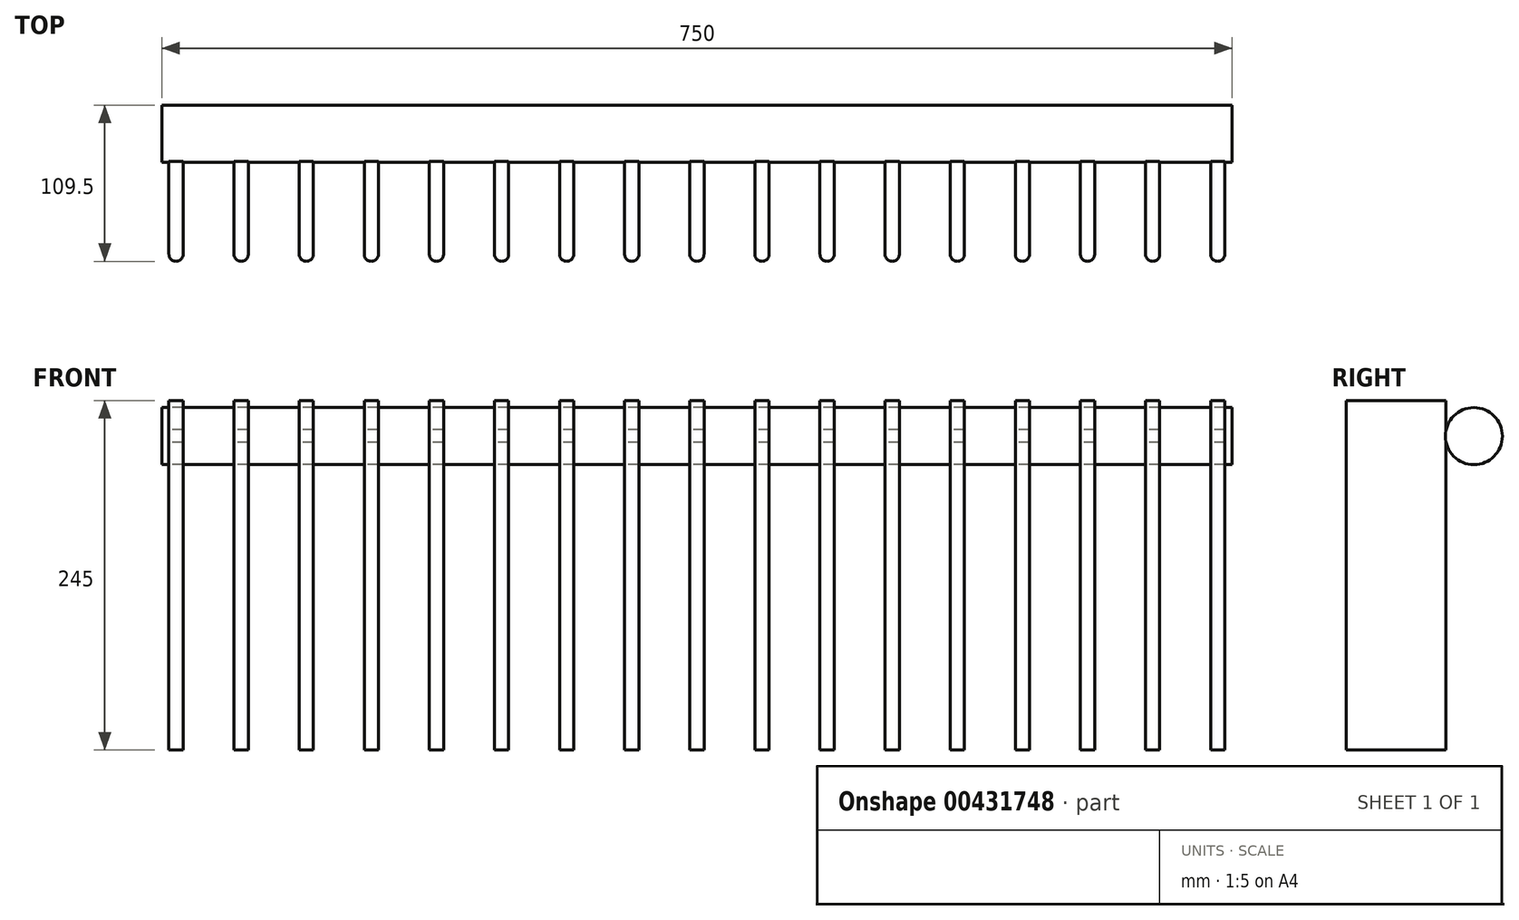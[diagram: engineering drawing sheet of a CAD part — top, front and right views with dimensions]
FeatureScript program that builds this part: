
annotation { "Feature Type Name" : "Feature", "Feature Type Description" : "" }
export const myFeature = defineFeature(function(context is Context, id is Id, definition is map)
    precondition{}
    {
        {
            var Q0;
            Q0=qCreatedBy(makeId("Right.planeOp"),FACE);
            var sketch = newSketch(context, id + "F0", { "sketchPlane" : qUnion([Q0])});
            skCircle(sketch, "E0", {"center": v(-45, 220) * mm, "radius": 20 * mm});
            skSolve(sketch);
        }
        {
            var Q0;
            Q0=makeQuery(id+"F0.imprint","IMPRINT",FACE,{"disambiguationData":[TD([[makeQuery(id+"F0.imprint","IMPRINT",EDGE,{"derivedFrom":sQuery(id+"F0.wireOp",EDGE,"E0")}),1.0]])]});
            extrude(context, id + "F1", {"entities" : qUnion([Q0]), "endBound" : BoundingType.SYMMETRIC, "depth" : 750 * mm});
        }
        {
            var Q0;
            Q0=qCreatedBy(makeId("Top.planeOp"),FACE);
            var Q1;
            Q1=sQuery(id+"F0.wireOp",VERTEX,"E0.center");
            cPlane(context, id + "F2", {"entities" : qUnion([Q0, Q1]), "cplaneType" : CPlaneType.PLANE_POINT, "offset" : 25 * mm, "width" : 150 * mm, "height" : 150 * mm});
        }
        {
            var Q0;
            Q0=qCreatedBy(id+"F2.planeOp",FACE);
            var sketch = newSketch(context, id + "F3", { "sketchPlane" : qUnion([Q0])});
            skLineSegment(sketch, "E1.bottom", {"start": v(-370, -64.5) * mm, "end": v(-360, -64.5) * mm});
            skLineSegment(sketch, "E1.top", {"start": v(-370, -134.5) * mm, "end": v(-360, -134.5) * mm});
            skLineSegment(sketch, "E1.left", {"start": v(-370, -64.5) * mm, "end": v(-370, -134.5) * mm});
            skLineSegment(sketch, "E1.right", {"start": v(-360, -64.5) * mm, "end": v(-360, -134.5) * mm});
            skLineSegment(sketch, "E2", {"start": v(-365, -64.5) * mm, "end": v(-365, -134.5) * mm, "construction": true});
            skLineSegment(sketch, "E3.1.0.0", {"start": v(-319.37, -64.5) * mm, "end": v(-319.37, -134.5) * mm, "construction": true});
            skLineSegment(sketch, "E3.1.0.1", {"start": v(-324.38, -64.5) * mm, "end": v(-324.38, -134.5) * mm});
            skLineSegment(sketch, "E3.1.0.2", {"start": v(-314.38, -64.5) * mm, "end": v(-314.38, -134.5) * mm});
            skLineSegment(sketch, "E3.1.0.3", {"start": v(-324.37, -134.5) * mm, "end": v(-314.37, -134.5) * mm});
            skLineSegment(sketch, "E3.1.0.4", {"start": v(-324.38, -64.5) * mm, "end": v(-314.37, -64.5) * mm});
            skLineSegment(sketch, "E3.2.0.0", {"start": v(-273.75, -64.5) * mm, "end": v(-273.75, -134.5) * mm, "construction": true});
            skLineSegment(sketch, "E3.2.0.1", {"start": v(-278.75, -64.5) * mm, "end": v(-278.75, -134.5) * mm});
            skLineSegment(sketch, "E3.2.0.2", {"start": v(-268.75, -64.5) * mm, "end": v(-268.75, -134.5) * mm});
            skLineSegment(sketch, "E3.2.0.3", {"start": v(-278.75, -134.5) * mm, "end": v(-268.75, -134.5) * mm});
            skLineSegment(sketch, "E3.2.0.4", {"start": v(-278.75, -64.5) * mm, "end": v(-268.75, -64.5) * mm});
            skLineSegment(sketch, "E3.3.0.0", {"start": v(-228.12, -64.5) * mm, "end": v(-228.12, -134.5) * mm, "construction": true});
            skLineSegment(sketch, "E3.3.0.1", {"start": v(-233.13, -64.5) * mm, "end": v(-233.13, -134.5) * mm});
            skLineSegment(sketch, "E3.3.0.2", {"start": v(-223.13, -64.5) * mm, "end": v(-223.13, -134.5) * mm});
            skLineSegment(sketch, "E3.3.0.3", {"start": v(-233.12, -134.5) * mm, "end": v(-223.12, -134.5) * mm});
            skLineSegment(sketch, "E3.3.0.4", {"start": v(-233.13, -64.5) * mm, "end": v(-223.12, -64.5) * mm});
            skLineSegment(sketch, "E3.4.0.0", {"start": v(-182.5, -64.5) * mm, "end": v(-182.5, -134.5) * mm, "construction": true});
            skLineSegment(sketch, "E3.4.0.1", {"start": v(-187.5, -64.5) * mm, "end": v(-187.5, -134.5) * mm});
            skLineSegment(sketch, "E3.4.0.2", {"start": v(-177.5, -64.5) * mm, "end": v(-177.5, -134.5) * mm});
            skLineSegment(sketch, "E3.4.0.3", {"start": v(-187.5, -134.5) * mm, "end": v(-177.5, -134.5) * mm});
            skLineSegment(sketch, "E3.4.0.4", {"start": v(-187.5, -64.5) * mm, "end": v(-177.5, -64.5) * mm});
            skLineSegment(sketch, "E3.5.0.0", {"start": v(-136.88, -64.5) * mm, "end": v(-136.88, -134.5) * mm, "construction": true});
            skLineSegment(sketch, "E3.5.0.1", {"start": v(-141.88, -64.5) * mm, "end": v(-141.88, -134.5) * mm});
            skLineSegment(sketch, "E3.5.0.2", {"start": v(-131.88, -64.5) * mm, "end": v(-131.88, -134.5) * mm});
            skLineSegment(sketch, "E3.5.0.3", {"start": v(-141.88, -134.5) * mm, "end": v(-131.88, -134.5) * mm});
            skLineSegment(sketch, "E3.5.0.4", {"start": v(-141.88, -64.5) * mm, "end": v(-131.87, -64.5) * mm});
            skLineSegment(sketch, "E3.6.0.0", {"start": v(-91.25, -64.5) * mm, "end": v(-91.25, -134.5) * mm, "construction": true});
            skLineSegment(sketch, "E3.6.0.1", {"start": v(-96.25, -64.5) * mm, "end": v(-96.25, -134.5) * mm});
            skLineSegment(sketch, "E3.6.0.2", {"start": v(-86.25, -64.5) * mm, "end": v(-86.25, -134.5) * mm});
            skLineSegment(sketch, "E3.6.0.3", {"start": v(-96.25, -134.5) * mm, "end": v(-86.25, -134.5) * mm});
            skLineSegment(sketch, "E3.6.0.4", {"start": v(-96.25, -64.5) * mm, "end": v(-86.25, -64.5) * mm});
            skLineSegment(sketch, "E3.7.0.0", {"start": v(-45.63, -64.5) * mm, "end": v(-45.63, -134.5) * mm, "construction": true});
            skLineSegment(sketch, "E3.7.0.1", {"start": v(-50.63, -64.5) * mm, "end": v(-50.63, -134.5) * mm});
            skLineSegment(sketch, "E3.7.0.2", {"start": v(-40.63, -64.5) * mm, "end": v(-40.63, -134.5) * mm});
            skLineSegment(sketch, "E3.7.0.3", {"start": v(-50.63, -134.5) * mm, "end": v(-40.63, -134.5) * mm});
            skLineSegment(sketch, "E3.7.0.4", {"start": v(-50.63, -64.5) * mm, "end": v(-40.62, -64.5) * mm});
            skLineSegment(sketch, "E3.8.0.0", {"start": v(0, -64.5) * mm, "end": v(0, -134.5) * mm, "construction": true});
            skLineSegment(sketch, "E3.8.0.1", {"start": v(-5, -64.5) * mm, "end": v(-5, -134.5) * mm});
            skLineSegment(sketch, "E3.8.0.2", {"start": v(5, -64.5) * mm, "end": v(5, -134.5) * mm});
            skLineSegment(sketch, "E3.8.0.3", {"start": v(-5, -134.5) * mm, "end": v(5, -134.5) * mm});
            skLineSegment(sketch, "E3.8.0.4", {"start": v(-5, -64.5) * mm, "end": v(5, -64.5) * mm});
            skLineSegment(sketch, "E3.9.0.0", {"start": v(45.63, -64.5) * mm, "end": v(45.63, -134.5) * mm, "construction": true});
            skLineSegment(sketch, "E3.9.0.1", {"start": v(40.62, -64.5) * mm, "end": v(40.62, -134.5) * mm});
            skLineSegment(sketch, "E3.9.0.2", {"start": v(50.62, -64.5) * mm, "end": v(50.63, -134.5) * mm});
            skLineSegment(sketch, "E3.9.0.3", {"start": v(40.63, -134.5) * mm, "end": v(50.63, -134.5) * mm});
            skLineSegment(sketch, "E3.9.0.4", {"start": v(40.62, -64.5) * mm, "end": v(50.63, -64.5) * mm});
            skLineSegment(sketch, "E3.10.0.0", {"start": v(91.25, -64.5) * mm, "end": v(91.25, -134.5) * mm, "construction": true});
            skLineSegment(sketch, "E3.10.0.1", {"start": v(86.25, -64.5) * mm, "end": v(86.25, -134.5) * mm});
            skLineSegment(sketch, "E3.10.0.2", {"start": v(96.25, -64.5) * mm, "end": v(96.25, -134.5) * mm});
            skLineSegment(sketch, "E3.10.0.3", {"start": v(86.25, -134.5) * mm, "end": v(96.25, -134.5) * mm});
            skLineSegment(sketch, "E3.10.0.4", {"start": v(86.25, -64.5) * mm, "end": v(96.25, -64.5) * mm});
            skLineSegment(sketch, "E3.11.0.0", {"start": v(136.87, -64.5) * mm, "end": v(136.87, -134.5) * mm, "construction": true});
            skLineSegment(sketch, "E3.11.0.1", {"start": v(131.87, -64.5) * mm, "end": v(131.87, -134.5) * mm});
            skLineSegment(sketch, "E3.11.0.2", {"start": v(141.87, -64.5) * mm, "end": v(141.87, -134.5) * mm});
            skLineSegment(sketch, "E3.11.0.3", {"start": v(131.87, -134.5) * mm, "end": v(141.87, -134.5) * mm});
            skLineSegment(sketch, "E3.11.0.4", {"start": v(131.87, -64.5) * mm, "end": v(141.88, -64.5) * mm});
            skLineSegment(sketch, "E3.12.0.0", {"start": v(182.5, -64.5) * mm, "end": v(182.5, -134.5) * mm, "construction": true});
            skLineSegment(sketch, "E3.12.0.1", {"start": v(177.5, -64.5) * mm, "end": v(177.5, -134.5) * mm});
            skLineSegment(sketch, "E3.12.0.2", {"start": v(187.5, -64.5) * mm, "end": v(187.5, -134.5) * mm});
            skLineSegment(sketch, "E3.12.0.3", {"start": v(177.5, -134.5) * mm, "end": v(187.5, -134.5) * mm});
            skLineSegment(sketch, "E3.12.0.4", {"start": v(177.5, -64.5) * mm, "end": v(187.5, -64.5) * mm});
            skLineSegment(sketch, "E3.13.0.0", {"start": v(228.13, -64.5) * mm, "end": v(228.13, -134.5) * mm, "construction": true});
            skLineSegment(sketch, "E3.13.0.1", {"start": v(223.12, -64.5) * mm, "end": v(223.12, -134.5) * mm});
            skLineSegment(sketch, "E3.13.0.2", {"start": v(233.12, -64.5) * mm, "end": v(233.12, -134.5) * mm});
            skLineSegment(sketch, "E3.13.0.3", {"start": v(223.13, -134.5) * mm, "end": v(233.13, -134.5) * mm});
            skLineSegment(sketch, "E3.13.0.4", {"start": v(223.12, -64.5) * mm, "end": v(233.13, -64.5) * mm});
            skLineSegment(sketch, "E3.14.0.0", {"start": v(273.75, -64.5) * mm, "end": v(273.75, -134.5) * mm, "construction": true});
            skLineSegment(sketch, "E3.14.0.1", {"start": v(268.75, -64.5) * mm, "end": v(268.75, -134.5) * mm});
            skLineSegment(sketch, "E3.14.0.2", {"start": v(278.75, -64.5) * mm, "end": v(278.75, -134.5) * mm});
            skLineSegment(sketch, "E3.14.0.3", {"start": v(268.75, -134.5) * mm, "end": v(278.75, -134.5) * mm});
            skLineSegment(sketch, "E3.14.0.4", {"start": v(268.75, -64.5) * mm, "end": v(278.75, -64.5) * mm});
            skLineSegment(sketch, "E3.15.0.0", {"start": v(319.37, -64.5) * mm, "end": v(319.37, -134.5) * mm, "construction": true});
            skLineSegment(sketch, "E3.15.0.1", {"start": v(314.37, -64.5) * mm, "end": v(314.37, -134.5) * mm});
            skLineSegment(sketch, "E3.15.0.2", {"start": v(324.37, -64.5) * mm, "end": v(324.38, -134.5) * mm});
            skLineSegment(sketch, "E3.15.0.3", {"start": v(314.37, -134.5) * mm, "end": v(324.37, -134.5) * mm});
            skLineSegment(sketch, "E3.15.0.4", {"start": v(314.37, -64.5) * mm, "end": v(324.38, -64.5) * mm});
            skLineSegment(sketch, "E3.16.0.0", {"start": v(365, -64.5) * mm, "end": v(365, -134.5) * mm, "construction": true});
            skLineSegment(sketch, "E3.16.0.1", {"start": v(360, -64.5) * mm, "end": v(360, -134.5) * mm});
            skLineSegment(sketch, "E3.16.0.2", {"start": v(370, -64.5) * mm, "end": v(370, -134.5) * mm});
            skLineSegment(sketch, "E3.16.0.3", {"start": v(360, -134.5) * mm, "end": v(370, -134.5) * mm});
            skLineSegment(sketch, "E3.16.0.4", {"start": v(360, -64.5) * mm, "end": v(370, -64.5) * mm});
            skLineSegment(sketch, "E3.direction1", {"start": v(-370, -134.5) * mm, "end": v(-324.37, -134.5) * mm, "construction": true});
            skSolve(sketch);
        }
        {
            var Q0;
            Q0 = qSketchRegion(id + "F3", true);
            var Q1;
            Q1=qCreatedBy(makeId("Top.planeOp"),FACE);
            extrude(context, id + "F4", {"entities" : qUnion([Q0]), "operationType" : NewBodyOperationType.ADD, "depth" : 25 * mm, "hasSecondDirection" : true, "secondDirectionBound" : SecondDirectionBoundingType.UP_TO_SURFACE, "secondDirectionOppositeDirection" : true, "secondDirectionBoundEntityFace" : qUnion([Q1]), "secondDirectionDepth" : 25 * mm});
        }
        {
            var Q0;
            Q0=makeQuery(id+"F4.opExtrude","SWEPT_EDGE",EDGE,{"disambiguationData":[OSD([sQuery(id+"F3.wireOp",EDGE,"E1.top"),sQuery(id+"F3.wireOp",EDGE,"E1.right")])]});
            var Q1;
            Q1=makeQuery(id+"F4.opExtrude","SWEPT_EDGE",EDGE,{"disambiguationData":[OSD([sQuery(id+"F3.wireOp",EDGE,"E1.top"),sQuery(id+"F3.wireOp",EDGE,"E1.left")])]});
            fillet(context, id + "F5", {"entities" : qUnion([Q0, Q1]), "radius" : 5 * mm, "tangentPropagation" : true, "allowEdgeOverflow" : false});
        }
        {
            var Q0;
            Q0=makeQuery(id+"F4.opExtrude","SWEPT_EDGE",EDGE,{"disambiguationData":[OSD([sQuery(id+"F3.wireOp",EDGE,"E3.1.0.1"),sQuery(id+"F3.wireOp",EDGE,"E3.1.0.3")])]});
            var Q1;
            Q1=makeQuery(id+"F4.opExtrude","SWEPT_EDGE",EDGE,{"disambiguationData":[OSD([sQuery(id+"F3.wireOp",EDGE,"E3.1.0.2"),sQuery(id+"F3.wireOp",EDGE,"E3.1.0.3")])]});
            var Q2;
            Q2=makeQuery(id+"F4.opExtrude","SWEPT_EDGE",EDGE,{"disambiguationData":[OSD([sQuery(id+"F3.wireOp",EDGE,"E3.2.0.1"),sQuery(id+"F3.wireOp",EDGE,"E3.2.0.3")])]});
            var Q3;
            Q3=makeQuery(id+"F4.opExtrude","SWEPT_EDGE",EDGE,{"disambiguationData":[OSD([sQuery(id+"F3.wireOp",EDGE,"E3.2.0.2"),sQuery(id+"F3.wireOp",EDGE,"E3.2.0.3")])]});
            var Q4;
            Q4=makeQuery(id+"F4.opExtrude","SWEPT_EDGE",EDGE,{"disambiguationData":[OSD([sQuery(id+"F3.wireOp",EDGE,"E3.3.0.2"),sQuery(id+"F3.wireOp",EDGE,"E3.3.0.3")])]});
            var Q5;
            Q5=makeQuery(id+"F4.opExtrude","SWEPT_EDGE",EDGE,{"disambiguationData":[OSD([sQuery(id+"F3.wireOp",EDGE,"E3.3.0.1"),sQuery(id+"F3.wireOp",EDGE,"E3.3.0.3")])]});
            var Q6;
            Q6=makeQuery(id+"F4.opExtrude","SWEPT_EDGE",EDGE,{"disambiguationData":[OSD([sQuery(id+"F3.wireOp",EDGE,"E3.4.0.2"),sQuery(id+"F3.wireOp",EDGE,"E3.4.0.3")])]});
            var Q7;
            Q7=makeQuery(id+"F4.opExtrude","SWEPT_EDGE",EDGE,{"disambiguationData":[OSD([sQuery(id+"F3.wireOp",EDGE,"E3.4.0.1"),sQuery(id+"F3.wireOp",EDGE,"E3.4.0.3")])]});
            var Q8;
            Q8=makeQuery(id+"F4.opExtrude","SWEPT_EDGE",EDGE,{"disambiguationData":[OSD([sQuery(id+"F3.wireOp",EDGE,"E3.5.0.2"),sQuery(id+"F3.wireOp",EDGE,"E3.5.0.3")])]});
            var Q9;
            Q9=makeQuery(id+"F4.opExtrude","SWEPT_EDGE",EDGE,{"disambiguationData":[OSD([sQuery(id+"F3.wireOp",EDGE,"E3.5.0.1"),sQuery(id+"F3.wireOp",EDGE,"E3.5.0.3")])]});
            var Q10;
            Q10=makeQuery(id+"F4.opExtrude","SWEPT_EDGE",EDGE,{"disambiguationData":[OSD([sQuery(id+"F3.wireOp",EDGE,"E3.6.0.2"),sQuery(id+"F3.wireOp",EDGE,"E3.6.0.3")])]});
            var Q11;
            Q11=makeQuery(id+"F4.opExtrude","SWEPT_EDGE",EDGE,{"disambiguationData":[OSD([sQuery(id+"F3.wireOp",EDGE,"E3.6.0.1"),sQuery(id+"F3.wireOp",EDGE,"E3.6.0.3")])]});
            var Q12;
            Q12=makeQuery(id+"F4.opExtrude","SWEPT_EDGE",EDGE,{"disambiguationData":[OSD([sQuery(id+"F3.wireOp",EDGE,"E3.7.0.2"),sQuery(id+"F3.wireOp",EDGE,"E3.7.0.3")])]});
            var Q13;
            Q13=makeQuery(id+"F4.opExtrude","SWEPT_EDGE",EDGE,{"disambiguationData":[OSD([sQuery(id+"F3.wireOp",EDGE,"E3.7.0.1"),sQuery(id+"F3.wireOp",EDGE,"E3.7.0.3")])]});
            var Q14;
            Q14=makeQuery(id+"F4.opExtrude","SWEPT_EDGE",EDGE,{"disambiguationData":[OSD([sQuery(id+"F3.wireOp",EDGE,"E3.8.0.2"),sQuery(id+"F3.wireOp",EDGE,"E3.8.0.3")])]});
            var Q15;
            Q15=makeQuery(id+"F4.opExtrude","SWEPT_EDGE",EDGE,{"disambiguationData":[OSD([sQuery(id+"F3.wireOp",EDGE,"E3.8.0.1"),sQuery(id+"F3.wireOp",EDGE,"E3.8.0.3")])]});
            var Q16;
            Q16=makeQuery(id+"F4.opExtrude","SWEPT_EDGE",EDGE,{"disambiguationData":[OSD([sQuery(id+"F3.wireOp",EDGE,"E3.9.0.2"),sQuery(id+"F3.wireOp",EDGE,"E3.9.0.3")])]});
            var Q17;
            Q17=makeQuery(id+"F4.opExtrude","SWEPT_EDGE",EDGE,{"disambiguationData":[OSD([sQuery(id+"F3.wireOp",EDGE,"E3.9.0.1"),sQuery(id+"F3.wireOp",EDGE,"E3.9.0.3")])]});
            var Q18;
            Q18=makeQuery(id+"F4.opExtrude","SWEPT_EDGE",EDGE,{"disambiguationData":[OSD([sQuery(id+"F3.wireOp",EDGE,"E3.10.0.1"),sQuery(id+"F3.wireOp",EDGE,"E3.10.0.3")])]});
            var Q19;
            Q19=makeQuery(id+"F4.opExtrude","SWEPT_EDGE",EDGE,{"disambiguationData":[OSD([sQuery(id+"F3.wireOp",EDGE,"E3.10.0.2"),sQuery(id+"F3.wireOp",EDGE,"E3.10.0.3")])]});
            var Q20;
            Q20=makeQuery(id+"F4.opExtrude","SWEPT_EDGE",EDGE,{"disambiguationData":[OSD([sQuery(id+"F3.wireOp",EDGE,"E3.11.0.1"),sQuery(id+"F3.wireOp",EDGE,"E3.11.0.3")])]});
            var Q21;
            Q21=makeQuery(id+"F4.opExtrude","SWEPT_EDGE",EDGE,{"disambiguationData":[OSD([sQuery(id+"F3.wireOp",EDGE,"E3.11.0.2"),sQuery(id+"F3.wireOp",EDGE,"E3.11.0.3")])]});
            var Q22;
            Q22=makeQuery(id+"F4.opExtrude","SWEPT_EDGE",EDGE,{"disambiguationData":[OSD([sQuery(id+"F3.wireOp",EDGE,"E3.12.0.2"),sQuery(id+"F3.wireOp",EDGE,"E3.12.0.3")])]});
            var Q23;
            Q23=makeQuery(id+"F4.opExtrude","SWEPT_EDGE",EDGE,{"disambiguationData":[OSD([sQuery(id+"F3.wireOp",EDGE,"E3.12.0.1"),sQuery(id+"F3.wireOp",EDGE,"E3.12.0.3")])]});
            var Q24;
            Q24=makeQuery(id+"F4.opExtrude","SWEPT_EDGE",EDGE,{"disambiguationData":[OSD([sQuery(id+"F3.wireOp",EDGE,"E3.13.0.2"),sQuery(id+"F3.wireOp",EDGE,"E3.13.0.3")])]});
            var Q25;
            Q25=makeQuery(id+"F4.opExtrude","SWEPT_EDGE",EDGE,{"disambiguationData":[OSD([sQuery(id+"F3.wireOp",EDGE,"E3.13.0.1"),sQuery(id+"F3.wireOp",EDGE,"E3.13.0.3")])]});
            var Q26;
            Q26=makeQuery(id+"F4.opExtrude","SWEPT_EDGE",EDGE,{"disambiguationData":[OSD([sQuery(id+"F3.wireOp",EDGE,"E3.14.0.2"),sQuery(id+"F3.wireOp",EDGE,"E3.14.0.3")])]});
            var Q27;
            Q27=makeQuery(id+"F4.opExtrude","SWEPT_EDGE",EDGE,{"disambiguationData":[OSD([sQuery(id+"F3.wireOp",EDGE,"E3.14.0.1"),sQuery(id+"F3.wireOp",EDGE,"E3.14.0.3")])]});
            var Q28;
            Q28=makeQuery(id+"F4.opExtrude","SWEPT_EDGE",EDGE,{"disambiguationData":[OSD([sQuery(id+"F3.wireOp",EDGE,"E3.15.0.2"),sQuery(id+"F3.wireOp",EDGE,"E3.15.0.3")])]});
            var Q29;
            Q29=makeQuery(id+"F4.opExtrude","SWEPT_EDGE",EDGE,{"disambiguationData":[OSD([sQuery(id+"F3.wireOp",EDGE,"E3.15.0.1"),sQuery(id+"F3.wireOp",EDGE,"E3.15.0.3")])]});
            var Q30;
            Q30=makeQuery(id+"F4.opExtrude","SWEPT_EDGE",EDGE,{"disambiguationData":[OSD([sQuery(id+"F3.wireOp",EDGE,"E3.16.0.2"),sQuery(id+"F3.wireOp",EDGE,"E3.16.0.3")])]});
            var Q31;
            Q31=makeQuery(id+"F4.opExtrude","SWEPT_EDGE",EDGE,{"disambiguationData":[OSD([sQuery(id+"F3.wireOp",EDGE,"E3.16.0.1"),sQuery(id+"F3.wireOp",EDGE,"E3.16.0.3")])]});
            var Q32;
            Q32=makeQuery(id+"F4.opExtrude","SWEPT_EDGE",EDGE,{"disambiguationData":[OSD([sQuery(id+"F3.wireOp",EDGE,"E3.17.0.2"),sQuery(id+"F3.wireOp",EDGE,"E3.17.0.3")])]});
            var Q33;
            Q33=makeQuery(id+"F4.opExtrude","SWEPT_EDGE",EDGE,{"disambiguationData":[OSD([sQuery(id+"F3.wireOp",EDGE,"E3.17.0.1"),sQuery(id+"F3.wireOp",EDGE,"E3.17.0.3")])]});
            var Q34;
            Q34=makeQuery(id+"F4.opExtrude","SWEPT_EDGE",EDGE,{"disambiguationData":[OSD([sQuery(id+"F3.wireOp",EDGE,"E3.18.0.2"),sQuery(id+"F3.wireOp",EDGE,"E3.18.0.3")])]});
            var Q35;
            Q35=makeQuery(id+"F4.opExtrude","SWEPT_EDGE",EDGE,{"disambiguationData":[OSD([sQuery(id+"F3.wireOp",EDGE,"E3.18.0.1"),sQuery(id+"F3.wireOp",EDGE,"E3.18.0.3")])]});
            var Q36;
            Q36=makeQuery(id+"F4.opExtrude","SWEPT_EDGE",EDGE,{"disambiguationData":[OSD([sQuery(id+"F3.wireOp",EDGE,"E3.19.0.2"),sQuery(id+"F3.wireOp",EDGE,"E3.19.0.3")])]});
            var Q37;
            Q37=makeQuery(id+"F4.opExtrude","SWEPT_EDGE",EDGE,{"disambiguationData":[OSD([sQuery(id+"F3.wireOp",EDGE,"E3.19.0.1"),sQuery(id+"F3.wireOp",EDGE,"E3.19.0.3")])]});
            fillet(context, id + "F6", {"entities" : qUnion([Q0, Q1, Q2, Q3, Q4, Q5, Q6, Q7, Q8, Q9, Q10, Q11, Q12, Q13, Q14, Q15, Q16, Q17, Q18, Q19, Q20, Q21, Q22, Q23, Q24, Q25, Q26, Q27, Q28, Q29, Q30, Q31, Q32, Q33, Q34, Q35, Q36, Q37]), "radius" : 5 * mm, "tangentPropagation" : true, "allowEdgeOverflow" : false});
        }
    });
